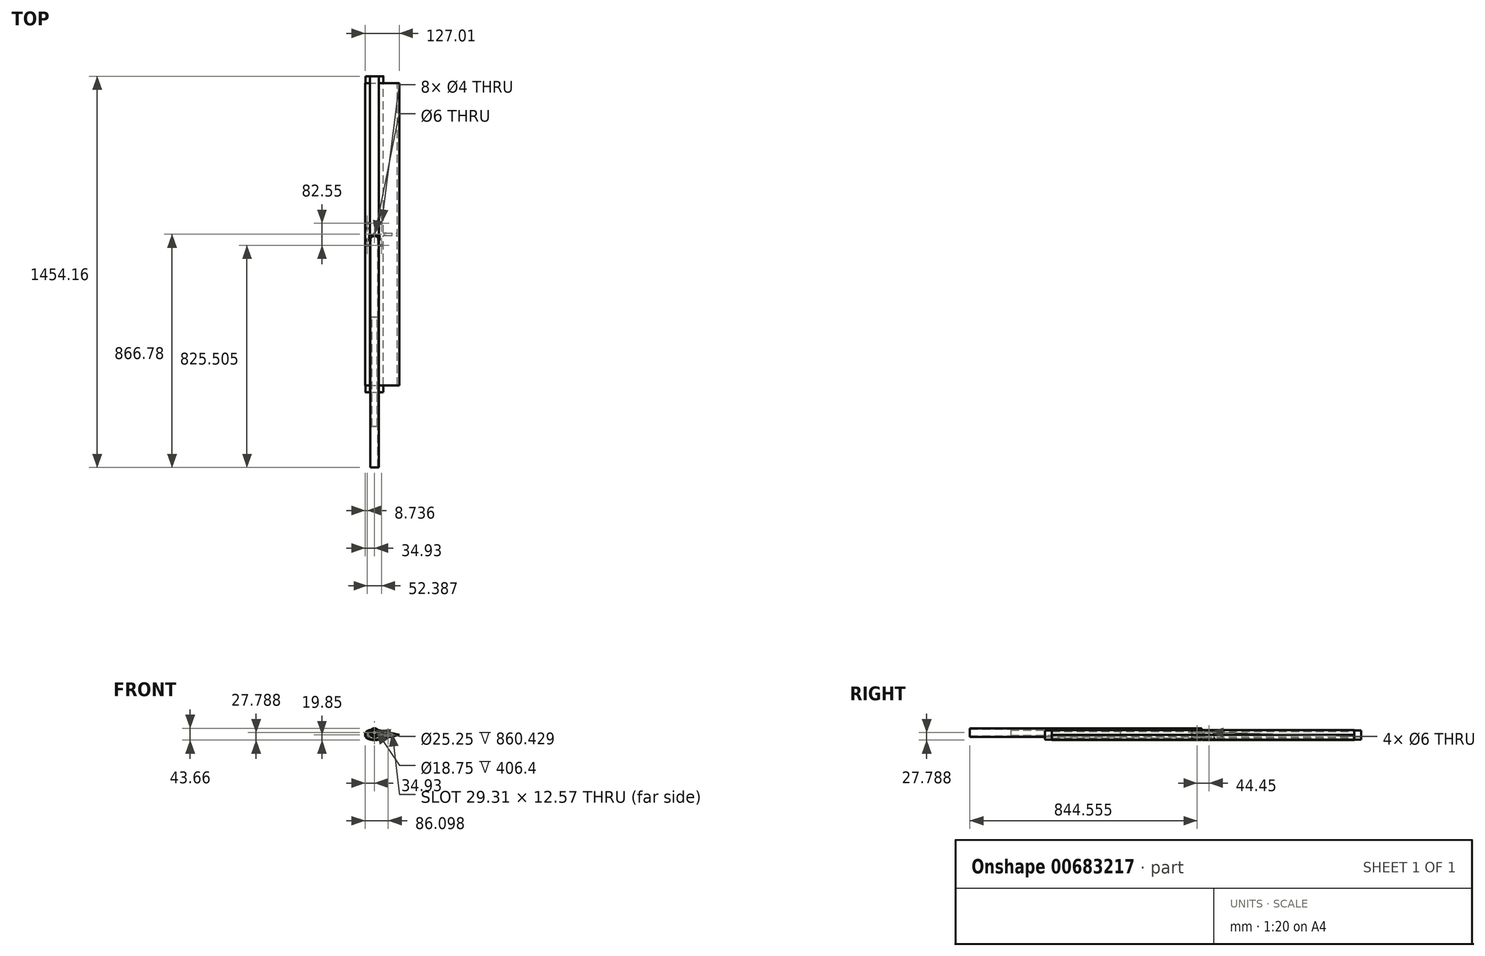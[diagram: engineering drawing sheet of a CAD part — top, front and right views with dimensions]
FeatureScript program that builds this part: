
annotation { "Feature Type Name" : "Feature", "Feature Type Description" : "" }
export const myFeature = defineFeature(function(context is Context, id is Id, definition is map)
    precondition{}
    {
        {
            var Q0;
            Q0=qCreatedBy(makeId("Front.planeOp"),FACE);
            var sketch = newSketch(context, id + "F0", { "sketchPlane" : qUnion([Q0])});
            skArc(sketch, "E0", {"start": v(-25.4, 14.55) * mm, "mid": v(-34.93, 0) * mm, "end": v(-25.4, -14.55) * mm});
            skArc(sketch, "E1", {"start": v(-25.4, 14.55) * mm, "mid": v(-21.1, 16.25) * mm, "end": v(-16.67, 17.62) * mm});
            skArc(sketch, "E2", {"start": v(-25.4, -14.55) * mm, "mid": v(-5.75, -19.59) * mm, "end": v(14.48, -18.18) * mm});
            skLineSegment(sketch, "E3", {"start": v(14.48, -16.55) * mm, "end": v(14.48, -18.18) * mm});
            skLineSegment(sketch, "E4", {"start": v(-16.67, 17.62) * mm, "end": v(-16.67, 7.94) * mm});
            skLineSegment(sketch, "E5", {"start": v(16.67, 16.03) * mm, "end": v(16.67, 7.94) * mm});
            skArc(sketch, "E6", {"start": v(-16.67, 7.94) * mm, "mid": v(0, -8.73) * mm, "end": v(16.67, 7.94) * mm});
            skLineSegment(sketch, "E7", {"start": v(14.48, -18.18) * mm, "end": v(92.08, 0) * mm});
            skLineSegment(sketch, "E8", {"start": v(16.67, 17.67) * mm, "end": v(92.07, 0) * mm});
            skLineSegment(sketch, "E9", {"start": v(16.67, 16.03) * mm, "end": v(16.67, 17.67) * mm});
            skLineSegment(sketch, "E10", {"start": v(85.12, 0) * mm, "end": v(92.07, 0) * mm});
            skLineSegment(sketch, "E11", {"start": v(-34.93, 22.71) * mm, "end": v(-34.93, 0) * mm, "construction": true});
            skLineSegment(sketch, "E12", {"start": v(33.34, 12.13) * mm, "end": v(33.34, -12.13) * mm});
            skLineSegment(sketch, "E13", {"start": v(14.48, -16.55) * mm, "end": v(33.34, -12.13) * mm});
            skLineSegment(sketch, "E14", {"start": v(33.34, -12.13) * mm, "end": v(85.12, 0) * mm});
            skLineSegment(sketch, "E15", {"start": v(16.67, 16.03) * mm, "end": v(33.34, 12.13) * mm});
            skLineSegment(sketch, "E16", {"start": v(33.34, 12.13) * mm, "end": v(85.12, 0) * mm});
            skArc(sketch, "E17", {"start": v(44.42, 6.27) * mm, "mid": v(36.51, 0) * mm, "end": v(44.42, -6.27) * mm});
            skArc(sketch, "E18", {"start": v(64.6, 1.55) * mm, "mid": v(65.82, 0) * mm, "end": v(64.6, -1.55) * mm});
            skLineSegment(sketch, "E19", {"start": v(44.42, 6.27) * mm, "end": v(64.6, 1.55) * mm});
            skLineSegment(sketch, "E20", {"start": v(44.42, -6.27) * mm, "end": v(64.6, -1.55) * mm});
            skLineSegment(sketch, "E21", {"start": v(36.51, 0) * mm, "end": v(36.51, 27.9) * mm, "construction": true});
            skPoint(sketch, "E21.startSnap0", {"position": v(36.51, 0) * mm});
            skPoint(sketch, "E22", {"position": v(33.34, 0) * mm});
            skSolve(sketch);
        }
        {
            var Q0;
            Q0=makeQuery(id+"F0.imprint","IMPRINT",FACE,{"disambiguationData":[TD([[makeQuery(id+"F0.imprint","IMPRINT",EDGE,{"derivedFrom":sQuery(id+"F0.wireOp",EDGE,"E0")}),1.0]])]});
            extrude(context, id + "F1", {"entities" : qUnion([Q0]), "endBound" : BoundingType.SYMMETRIC, "depth" : 1123.95 * mm, "offsetDistance" : 25.4 * mm});
        }
        {
            var Q0;
            Q0=makeQuery(id+"F0.imprint","IMPRINT",FACE,{"disambiguationData":[TD([[makeQuery(id+"F0.imprint","IMPRINT",EDGE,{"derivedFrom":sQuery(id+"F0.wireOp",EDGE,"E8")}),-1.0]])]});
            extrude(context, id + "F2", {"entities" : qUnion([Q0]), "endBound" : BoundingType.SYMMETRIC, "depth" : 1123.95 * mm, "offsetDistance" : 25.4 * mm});
        }
        {
            var Q0;
            Q0=makeQuery(id+"F0.imprint","IMPRINT",FACE,{"disambiguationData":[TD([[makeQuery(id+"F0.imprint","IMPRINT",EDGE,{"derivedFrom":sQuery(id+"F0.wireOp",EDGE,"E3")}),1.0]])]});
            extrude(context, id + "F3", {"entities" : qUnion([Q0]), "endBound" : BoundingType.SYMMETRIC, "depth" : 1123.95 * mm, "offsetDistance" : 25.4 * mm});
        }
        {
            var Q0;
            Q0=makeQuery(id+"F0.imprint","IMPRINT",FACE,{"disambiguationData":[TD([[makeQuery(id+"F0.imprint","IMPRINT",EDGE,{"derivedFrom":sQuery(id+"F0.wireOp",EDGE,"E12")}),1.0]])]});
            extrude(context, id + "F4", {"entities" : qUnion([Q0]), "endBound" : BoundingType.SYMMETRIC, "depth" : 9.52 * mm, "offsetDistance" : 25.4 * mm});
        }
        {
            var Q0;
            Q0=makeQuery(id+"F1.opExtrude","CAP_FACE",FACE,{"disambiguationData":[OSD([sQuery(id+"F0.wireOp",EDGE,"E0"),sQuery(id+"F0.wireOp",EDGE,"E1"),sQuery(id+"F0.wireOp",EDGE,"E2"),sQuery(id+"F0.wireOp",EDGE,"E3"),sQuery(id+"F0.wireOp",EDGE,"E4"),sQuery(id+"F0.wireOp",EDGE,"E5"),sQuery(id+"F0.wireOp",EDGE,"E6"),sQuery(id+"F0.wireOp",EDGE,"E12"),sQuery(id+"F0.wireOp",EDGE,"E13"),sQuery(id+"F0.wireOp",EDGE,"E15")])],"isStart":false});
            var sketch = newSketch(context, id + "F5", { "sketchPlane" : qUnion([Q0])});
            skArc(sketch, "E23", {"start": v(-16.67, 7.94) * mm, "mid": v(0, -8.73) * mm, "end": v(16.67, 7.94) * mm});
            skArc(sketch, "E24", {"start": v(-24.77, 13.1) * mm, "mid": v(-33.34, 0) * mm, "end": v(-24.77, -13.1) * mm});
            skArc(sketch, "E25", {"start": v(24.77, 13.1) * mm, "mid": v(33.34, 0) * mm, "end": v(24.77, -13.1) * mm});
            skLineSegment(sketch, "E26", {"start": v(-16.67, 7.94) * mm, "end": v(-16.67, 15.98) * mm});
            skLineSegment(sketch, "E27", {"start": v(16.67, 7.94) * mm, "end": v(16.67, 15.98) * mm});
            skPoint(sketch, "E27.endSnap0", {"position": v(16.67, 15.98) * mm});
            skArc(sketch, "E28", {"start": v(-24.77, -13.1) * mm, "mid": v(0, -18.26) * mm, "end": v(24.77, -13.1) * mm});
            skArc(sketch, "E29", {"start": v(-24.77, 13.1) * mm, "mid": v(-20.77, 14.68) * mm, "end": v(-16.67, 15.98) * mm});
            skArc(sketch, "E30", {"start": v(24.77, 13.1) * mm, "mid": v(20.77, 14.68) * mm, "end": v(16.67, 15.98) * mm});
            skLineSegment(sketch, "E31", {"start": v(-33.34, 8.6) * mm, "end": v(-33.34, 0) * mm, "construction": true});
            skLineSegment(sketch, "E32", {"start": v(33.34, 8.6) * mm, "end": v(33.34, 0) * mm, "construction": true});
            skSolve(sketch);
        }
        {
            var Q0;
            Q0=makeQuery(id+"F5.imprint","IMPRINT",FACE,{"disambiguationData":[TD([[makeQuery(id+"F5.imprint","IMPRINT",EDGE,{"derivedFrom":sQuery(id+"F5.wireOp",EDGE,"E23")}),-1.0]])]});
            extrude(context, id + "F6", {"entities" : qUnion([Q0]), "operationType" : NewBodyOperationType.ADD, "depth" : 25.4 * mm, "offsetDistance" : 25.4 * mm});
        }
        {
            var Q0;
            Q0 = qSketchRegion(id + "F5", true);
            extrude(context, id + "F7", {"entities" : qUnion([Q0]), "operationType" : NewBodyOperationType.ADD, "oppositeDirection" : true, "depth" : 1149.35 * mm, "offsetDistance" : 25.4 * mm});
        }
        {
            var Q0;
            Q0=qCreatedBy(makeId("Right.planeOp"),FACE);
            var sketch = newSketch(context, id + "F8", { "sketchPlane" : qUnion([Q0])});
            skCircle(sketch, "E33", {"center": v(-22.23, 7.94) * mm, "radius": 3 * mm});
            skCircle(sketch, "E34", {"center": v(22.23, 7.94) * mm, "radius": 3 * mm});
            skLineSegment(sketch, "E35", {"start": v(-22.23, 7.94) * mm, "end": v(22.23, 7.94) * mm, "construction": true});
            skSolve(sketch);
        }
        {
            var Q0;
            Q0 = qSketchRegion(id + "F8", true);
            extrude(context, id + "F9", {"entities" : qUnion([Q0]), "operationType" : NewBodyOperationType.REMOVE, "oppositeDirection" : true, "depth" : 50.8 * mm, "offsetDistance" : 25.4 * mm, "hasSecondDirection" : true, "secondDirectionOppositeDirection" : false, "secondDirectionDepth" : 19.05 * mm});
        }
        {
            var Q0;
            Q0=qCreatedBy(makeId("Top.planeOp"),FACE);
            var sketch = newSketch(context, id + "F10", { "sketchPlane" : qUnion([Q0])});
            skCircle(sketch, "E36", {"center": v(0, 0) * mm, "radius": 3 * mm});
            skCircle(sketch, "E37", {"center": v(-26.2, 41.28) * mm, "radius": 2 * mm});
            skCircle(sketch, "E38", {"center": v(26.2, 41.28) * mm, "radius": 2 * mm});
            skCircle(sketch, "E39", {"center": v(-26.2, -41.27) * mm, "radius": 2 * mm});
            skCircle(sketch, "E40", {"center": v(26.2, -41.28) * mm, "radius": 2 * mm});
            skLineSegment(sketch, "E41", {"start": v(-26.2, 41.28) * mm, "end": v(26.2, 41.28) * mm, "construction": true});
            skLineSegment(sketch, "E42", {"start": v(26.2, 41.28) * mm, "end": v(26.2, -41.28) * mm, "construction": true});
            skLineSegment(sketch, "E43", {"start": v(-26.2, 41.28) * mm, "end": v(-26.2, -41.27) * mm, "construction": true});
            skLineSegment(sketch, "E44", {"start": v(0, 41.28) * mm, "end": v(0, -41.28) * mm, "construction": true});
            skSolve(sketch);
        }
        {
            var Q0;
            Q0 = qSketchRegion(id + "F10", true);
            extrude(context, id + "F11", {"entities" : qUnion([Q0]), "operationType" : NewBodyOperationType.REMOVE, "endBound" : BoundingType.SYMMETRIC, "oppositeDirection" : true, "depth" : 50.8 * mm, "offsetDistance" : 25.4 * mm});
        }
        {
            var Q0;
            Q0=makeQuery(id+"F10.imprint","IMPRINT",FACE,{"disambiguationData":[TD([[makeQuery(id+"F10.imprint","IMPRINT",EDGE,{"derivedFrom":sQuery(id+"F10.wireOp",EDGE,"E38")}),1.0]])]});
            var Q1;
            Q1=makeQuery(id+"F10.imprint","IMPRINT",FACE,{"disambiguationData":[TD([[makeQuery(id+"F10.imprint","IMPRINT",EDGE,{"derivedFrom":sQuery(id+"F10.wireOp",EDGE,"E40")}),1.0]])]});
            var Q2;
            Q2=sQuery(id+"F10.wireOp",EDGE,"E38");
            var Q3;
            Q3=sQuery(id+"F10.wireOp",EDGE,"E40");
            extrude(context, id + "F12", {"entities" : qUnion([Q0, Q1]), "operationType" : NewBodyOperationType.REMOVE, "surfaceEntities" : qUnion([Q2, Q3]), "endBound" : BoundingType.SYMMETRIC, "depth" : 50.8 * mm, "offsetDistance" : 25.4 * mm});
        }
        {
            var Q0;
            Q0=qCreatedBy(makeId("Right.planeOp"),FACE);
            var sketch = newSketch(context, id + "F13", { "sketchPlane" : qUnion([Q0])});
            skLineSegment(sketch, "E45", {"start": v(-6.35, 23.81) * mm, "end": v(-866.78, 23.81) * mm});
            skLineSegment(sketch, "E46", {"start": v(-866.78, 23.81) * mm, "end": v(-866.78, 20.56) * mm});
            skLineSegment(sketch, "E47", {"start": v(-866.78, 20.56) * mm, "end": v(-6.35, 20.56) * mm});
            skLineSegment(sketch, "E48", {"start": v(-6.35, 20.56) * mm, "end": v(-6.35, 23.81) * mm});
            skLineSegment(sketch, "E49", {"start": v(-6.35, 23.81) * mm, "end": v(-6.35, 7.94) * mm, "construction": true});
            skLineSegment(sketch, "E50", {"start": v(-714.38, 20.56) * mm, "end": v(-714.38, 17.31) * mm});
            skLineSegment(sketch, "E51", {"start": v(-714.38, 17.31) * mm, "end": v(-307.98, 17.31) * mm});
            skLineSegment(sketch, "E52", {"start": v(-307.98, 17.31) * mm, "end": v(-307.98, 20.56) * mm});
            skLineSegment(sketch, "E53", {"start": v(-307.98, 20.56) * mm, "end": v(-714.38, 20.56) * mm});
            skLineSegment(sketch, "E54", {"start": v(-6.35, 7.94) * mm, "end": v(-872.82, 7.94) * mm, "construction": true});
            skSolve(sketch);
        }
        {
            var Q0;
            Q0=makeQuery(id+"F13.imprint","IMPRINT",FACE,{"disambiguationData":[TD([[makeQuery(id+"F13.imprint","IMPRINT",EDGE,{"derivedFrom":sQuery(id+"F13.wireOp",EDGE,"E45")}),1.0]])]});
            var Q1;
            Q1=sQuery(id+"F13.wireOp",EDGE,"E54");
            revolve(context, id + "F14", {"entities" : qUnion([Q0]), "axis" : qUnion([Q1]), "revolveType" : RevolveType.FULL});
        }
        {
            var Q0;
            Q0=makeQuery(id+"F13.imprint","IMPRINT",FACE,{"disambiguationData":[TD([[makeQuery(id+"F13.imprint","IMPRINT",EDGE,{"derivedFrom":sQuery(id+"F13.wireOp",EDGE,"E50")}),1.0]])]});
            var Q1;
            Q1=sQuery(id+"F13.wireOp",EDGE,"E54");
            revolve(context, id + "F15", {"entities" : qUnion([Q0]), "axis" : qUnion([Q1]), "revolveType" : RevolveType.FULL});
        }
        {
            var Q0;
            Q0=makeQuery(id+"F8.imprint","IMPRINT",FACE,{"disambiguationData":[TD([[makeQuery(id+"F8.imprint","IMPRINT",EDGE,{"derivedFrom":sQuery(id+"F8.wireOp",EDGE,"E33")}),1.0]])]});
            var Q1;
            Q1=sQuery(id+"F8.wireOp",EDGE,"E33");
            extrude(context, id + "F16", {"entities" : qUnion([Q0]), "operationType" : NewBodyOperationType.REMOVE, "surfaceEntities" : qUnion([Q1]), "endBound" : BoundingType.SYMMETRIC, "oppositeDirection" : true, "depth" : 38.1 * mm, "offsetDistance" : 25.4 * mm});
        }
        {
            var Q0;
            Q0=qCreatedBy(makeId("Top.planeOp"),FACE);
            var sketch = newSketch(context, id + "F17", { "sketchPlane" : qUnion([Q0])});
            skArc(sketch, "E55", {"start": v(15.88, -22.23) * mm, "mid": v(0, -6.35) * mm, "end": v(-15.88, -22.22) * mm});
            skLineSegment(sketch, "E56", {"start": v(-15.88, -22.23) * mm, "end": v(-19.05, -22.23) * mm});
            skLineSegment(sketch, "E57", {"start": v(-19.05, -22.23) * mm, "end": v(-19.05, -3.18) * mm});
            skLineSegment(sketch, "E58", {"start": v(-19.05, -3.18) * mm, "end": v(19.05, -3.18) * mm});
            skLineSegment(sketch, "E59", {"start": v(19.05, -3.18) * mm, "end": v(19.05, -22.23) * mm});
            skLineSegment(sketch, "E60", {"start": v(19.05, -22.22) * mm, "end": v(15.88, -22.22) * mm});
            skLineSegment(sketch, "E61", {"start": v(-16.67, -22.23) * mm, "end": v(16.67, -22.23) * mm, "construction": true});
            skSolve(sketch);
        }
        {
            var Q0;
            Q0=makeQuery(id+"F17.imprint","IMPRINT",FACE,{"disambiguationData":[TD([[makeQuery(id+"F17.imprint","IMPRINT",EDGE,{"derivedFrom":sQuery(id+"F17.wireOp",EDGE,"E55")}),-1.0]])]});
            extrude(context, id + "F18", {"entities" : qUnion([Q0]), "operationType" : NewBodyOperationType.REMOVE, "endBound" : BoundingType.SYMMETRIC, "oppositeDirection" : true, "depth" : 50.8 * mm, "offsetDistance" : 25.4 * mm});
        }
    });
